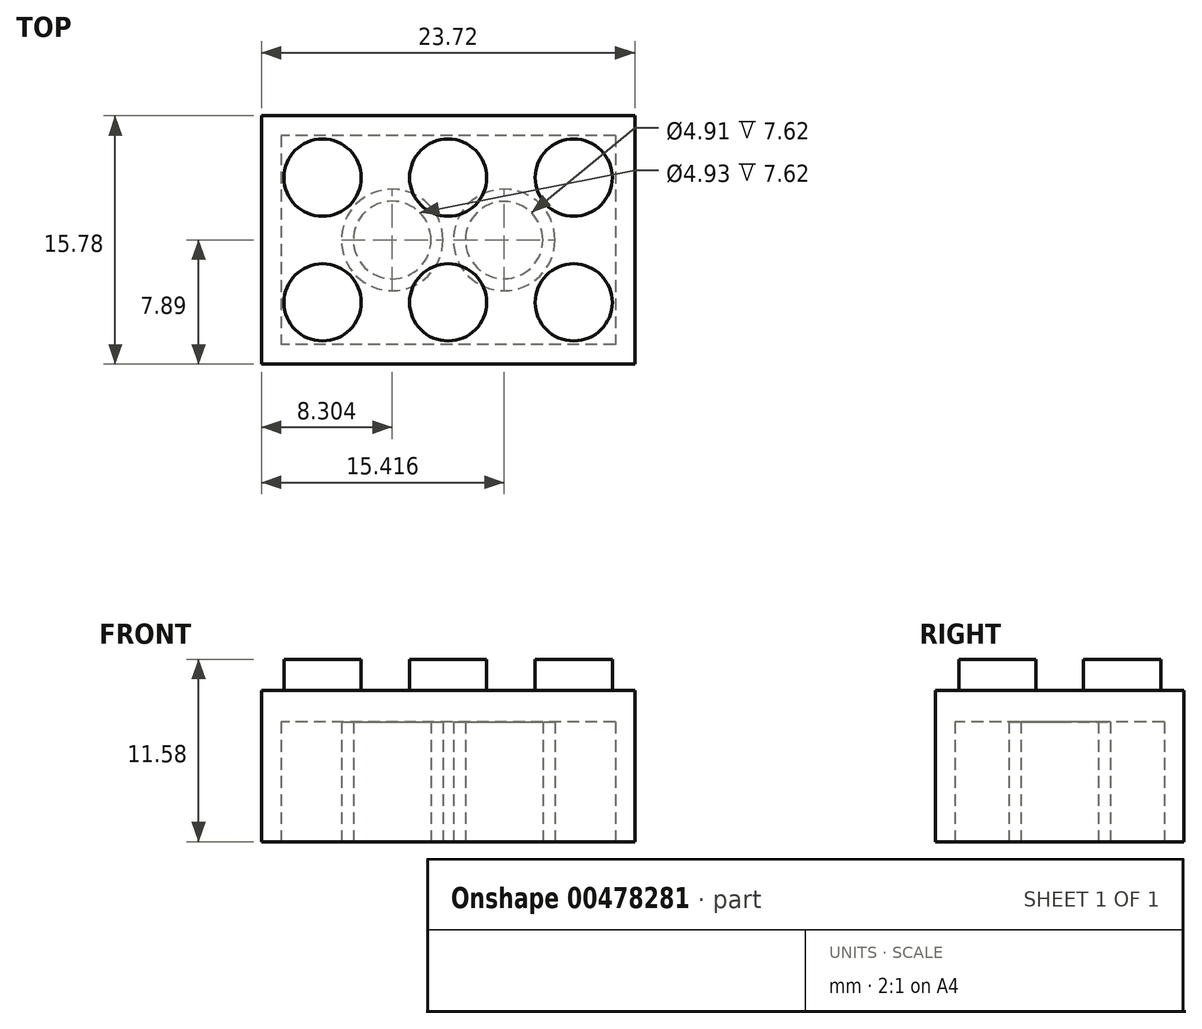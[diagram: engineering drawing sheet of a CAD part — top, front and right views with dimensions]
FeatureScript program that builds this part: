
annotation { "Feature Type Name" : "Feature", "Feature Type Description" : "" }
export const myFeature = defineFeature(function(context is Context, id is Id, definition is map)
    precondition{}
    {
        {
            var Q0;
            Q0=qCreatedBy(makeId("Top.planeOp"),FACE);
            var sketch = newSketch(context, id + "F0", { "sketchPlane" : qUnion([Q0])});
            skLineSegment(sketch, "E0.bottom", {"start": v(-11.86, -7.89) * mm, "end": v(11.86, -7.89) * mm});
            skLineSegment(sketch, "E0.top", {"start": v(-11.86, 7.89) * mm, "end": v(11.86, 7.89) * mm});
            skLineSegment(sketch, "E0.left", {"start": v(-11.86, -7.89) * mm, "end": v(-11.86, 7.89) * mm});
            skLineSegment(sketch, "E0.right", {"start": v(11.86, -7.89) * mm, "end": v(11.86, 7.89) * mm});
            skPoint(sketch, "E0.middle", {"position": v(0, 0) * mm});
            skSolve(sketch);
        }
        {
            var Q0;
            Q0=makeQuery(id+"F0.imprint","IMPRINT",FACE,{"disambiguationData":[TD([[makeQuery(id+"F0.imprint","IMPRINT",EDGE,{"derivedFrom":sQuery(id+"F0.wireOp",EDGE,"E0.bottom")}),1.0]])]});
            var sketch = newSketch(context, id + "F1", { "sketchPlane" : qUnion([Q0])});
            skCircle(sketch, "E1", {"center": v(-7.98, 3.96) * mm, "radius": 2.45 * mm});
            skCircle(sketch, "E2", {"center": v(-7.98, -3.96) * mm, "radius": 2.45 * mm});
            skCircle(sketch, "E3", {"center": v(0, -3.96) * mm, "radius": 2.45 * mm});
            skCircle(sketch, "E4", {"center": v(7.98, -3.96) * mm, "radius": 2.45 * mm});
            skCircle(sketch, "E5", {"center": v(7.98, 3.96) * mm, "radius": 2.45 * mm});
            skCircle(sketch, "E6", {"center": v(0, 3.96) * mm, "radius": 2.45 * mm});
            skSolve(sketch);
        }
        {
            var Q0;
            Q0=makeQuery(id+"F0.imprint","IMPRINT",FACE,{"disambiguationData":[TD([[makeQuery(id+"F0.imprint","IMPRINT",EDGE,{"derivedFrom":sQuery(id+"F0.wireOp",EDGE,"E0.bottom")}),1.0]])]});
            extrude(context, id + "F2", {"entities" : qUnion([Q0]), "oppositeDirection" : true, "depth" : 9.6 * mm, "offsetDistance" : 25.4 * mm});
        }
        {
            var Q0;
            Q0=makeQuery(id+"F1.imprint","IMPRINT",FACE,{"disambiguationData":[TD([[makeQuery(id+"F1.imprint","IMPRINT",EDGE,{"derivedFrom":sQuery(id+"F1.wireOp",EDGE,"E1")}),1.0]])]});
            var Q1;
            Q1=makeQuery(id+"F1.imprint","IMPRINT",FACE,{"disambiguationData":[TD([[makeQuery(id+"F1.imprint","IMPRINT",EDGE,{"derivedFrom":sQuery(id+"F1.wireOp",EDGE,"E6")}),1.0]])]});
            var Q2;
            Q2=makeQuery(id+"F1.imprint","IMPRINT",FACE,{"disambiguationData":[TD([[makeQuery(id+"F1.imprint","IMPRINT",EDGE,{"derivedFrom":sQuery(id+"F1.wireOp",EDGE,"E5")}),1.0]])]});
            var Q3;
            Q3=makeQuery(id+"F1.imprint","IMPRINT",FACE,{"disambiguationData":[TD([[makeQuery(id+"F1.imprint","IMPRINT",EDGE,{"derivedFrom":sQuery(id+"F1.wireOp",EDGE,"E4")}),1.0]])]});
            var Q4;
            Q4=makeQuery(id+"F1.imprint","IMPRINT",FACE,{"disambiguationData":[TD([[makeQuery(id+"F1.imprint","IMPRINT",EDGE,{"derivedFrom":sQuery(id+"F1.wireOp",EDGE,"E3")}),1.0]])]});
            var Q5;
            Q5=makeQuery(id+"F1.imprint","IMPRINT",FACE,{"disambiguationData":[TD([[makeQuery(id+"F1.imprint","IMPRINT",EDGE,{"derivedFrom":sQuery(id+"F1.wireOp",EDGE,"E2")}),1.0]])]});
            extrude(context, id + "F3", {"entities" : qUnion([Q0, Q1, Q2, Q3, Q4, Q5]), "operationType" : NewBodyOperationType.ADD, "depth" : 1.98 * mm, "offsetDistance" : 25.4 * mm});
        }
        {
            var Q0;
            Q0=makeQuery(id+"F2.opExtrude","CAP_FACE",FACE,{"disambiguationData":[OSD([sQuery(id+"F0.wireOp",EDGE,"E0.bottom"),sQuery(id+"F0.wireOp",EDGE,"E0.top"),sQuery(id+"F0.wireOp",EDGE,"E0.left"),sQuery(id+"F0.wireOp",EDGE,"E0.right")])],"isStart":false});
            var sketch = newSketch(context, id + "F4", { "sketchPlane" : qUnion([Q0])});
            skLineSegment(sketch, "E7.bottom", {"start": v(10.62, -6.64) * mm, "end": v(-10.62, -6.64) * mm});
            skLineSegment(sketch, "E7.top", {"start": v(10.62, 6.64) * mm, "end": v(-10.62, 6.64) * mm});
            skLineSegment(sketch, "E7.left", {"start": v(10.62, -6.64) * mm, "end": v(10.62, 6.64) * mm});
            skLineSegment(sketch, "E7.right", {"start": v(-10.62, -6.64) * mm, "end": v(-10.62, 6.64) * mm});
            skPoint(sketch, "E7.middle", {"position": v(0, 0) * mm});
            skSolve(sketch);
        }
        {
            var Q0;
            Q0=makeQuery(id+"F4.imprint","IMPRINT",FACE,{"disambiguationData":[TD([[makeQuery(id+"F4.imprint","IMPRINT",EDGE,{"derivedFrom":sQuery(id+"F4.wireOp",EDGE,"E7.bottom")}),-1.0]])]});
            var sketch = newSketch(context, id + "F5", { "sketchPlane" : qUnion([Q0])});
            skCircle(sketch, "E8", {"center": v(-3.56, 0) * mm, "radius": 3.23 * mm});
            skCircle(sketch, "E9", {"center": v(3.56, 0) * mm, "radius": 3.23 * mm});
            skSolve(sketch);
        }
        {
            var Q0;
            Q0=makeQuery(id+"F4.imprint","IMPRINT",FACE,{"disambiguationData":[TD([[makeQuery(id+"F4.imprint","IMPRINT",EDGE,{"derivedFrom":sQuery(id+"F4.wireOp",EDGE,"E7.bottom")}),-1.0]])]});
            extrude(context, id + "F6", {"entities" : qUnion([Q0]), "operationType" : NewBodyOperationType.REMOVE, "oppositeDirection" : true, "depth" : 7.62 * mm, "offsetDistance" : 25.4 * mm});
        }
        {
            var Q0;
            Q0=makeQuery(id+"F5.imprint","IMPRINT",FACE,{"disambiguationData":[TD([[makeQuery(id+"F5.imprint","IMPRINT",EDGE,{"derivedFrom":sQuery(id+"F5.wireOp",EDGE,"E8")}),1.0]])]});
            var Q1;
            Q1=makeQuery(id+"F5.imprint","IMPRINT",FACE,{"disambiguationData":[TD([[makeQuery(id+"F5.imprint","IMPRINT",EDGE,{"derivedFrom":sQuery(id+"F5.wireOp",EDGE,"E9")}),1.0]])]});
            extrude(context, id + "F7", {"entities" : qUnion([Q0, Q1]), "operationType" : NewBodyOperationType.ADD, "oppositeDirection" : true, "depth" : 8.9 * mm, "offsetDistance" : 25.4 * mm});
        }
        {
            var Q0;
            Q0=makeQuery(id+"F7.opExtrude","CAP_FACE",FACE,{"disambiguationData":[OSD([sQuery(id+"F5.wireOp",EDGE,"E8")])],"isStart":true});
            var sketch = newSketch(context, id + "F8", { "sketchPlane" : qUnion([Q0])});
            skCircle(sketch, "E10", {"center": v(-3.56, 0) * mm, "radius": 2.47 * mm});
            skSolve(sketch);
        }
        {
            var Q0;
            Q0=makeQuery(id+"F7.opExtrude","CAP_FACE",FACE,{"disambiguationData":[OSD([sQuery(id+"F5.wireOp",EDGE,"E9")])],"isStart":true});
            var sketch = newSketch(context, id + "F9", { "sketchPlane" : qUnion([Q0])});
            skCircle(sketch, "E11", {"center": v(3.56, 0) * mm, "radius": 2.46 * mm});
            skSolve(sketch);
        }
        {
            var Q0;
            Q0=makeQuery(id+"F8.imprint","IMPRINT",FACE,{"disambiguationData":[TD([[makeQuery(id+"F8.imprint","IMPRINT",EDGE,{"derivedFrom":sQuery(id+"F8.wireOp",EDGE,"E10")}),1.0]])]});
            var Q1;
            Q1=makeQuery(id+"F9.imprint","IMPRINT",FACE,{"disambiguationData":[TD([[makeQuery(id+"F9.imprint","IMPRINT",EDGE,{"derivedFrom":sQuery(id+"F9.wireOp",EDGE,"E11")}),1.0]])]});
            extrude(context, id + "F10", {"entities" : qUnion([Q0, Q1]), "operationType" : NewBodyOperationType.REMOVE, "oppositeDirection" : true, "depth" : 7.62 * mm, "offsetDistance" : 25.4 * mm});
        }
    });
